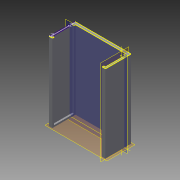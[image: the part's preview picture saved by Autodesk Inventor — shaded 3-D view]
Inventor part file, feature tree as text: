
AUTODESK INVENTOR PART (.ipt)
format: ipt  version: 2015 (Build 190159000, 159)  size: 148,480 bytes
history: native  units: mm
features: sketch x4, projected_geometry x4, extrude x3
ambient origin geometry x8: Origin, YZ Plane, XZ Plane, XY Plane, X Axis, Y Axis, Z Axis, Center Point
bodies: Solid1 (feature_tree)
feature tree (11):
  extrude  "Extrusion1"  Depth=24.0mm
  extrude  "Extrusion2"  Depth=2.0mm
  extrude  "Extrusion3"  Depth=3.0mm TaperAngle=0.0deg
  sketch  "Sketch5"  dims[d8=2.0mm d9=0.0mm d10=2.0mm d11=2.0mm]
  sketch  "Sketch1"  dims[d0=2.0mm d1=24.0mm]
  sketch  "Sketch3"  dims[d2=2.0mm d3=32.0mm]
  projected_geometry  "Projected Loop1"
  projected_geometry  "Projected Loop2"
  sketch  "Sketch4"  dims[d4=94.2mm d5=0.0mm d6=3.0mm d7=0.0mm]
  projected_geometry  "Projected Loop3"
  projected_geometry  "Projected Loop4"
